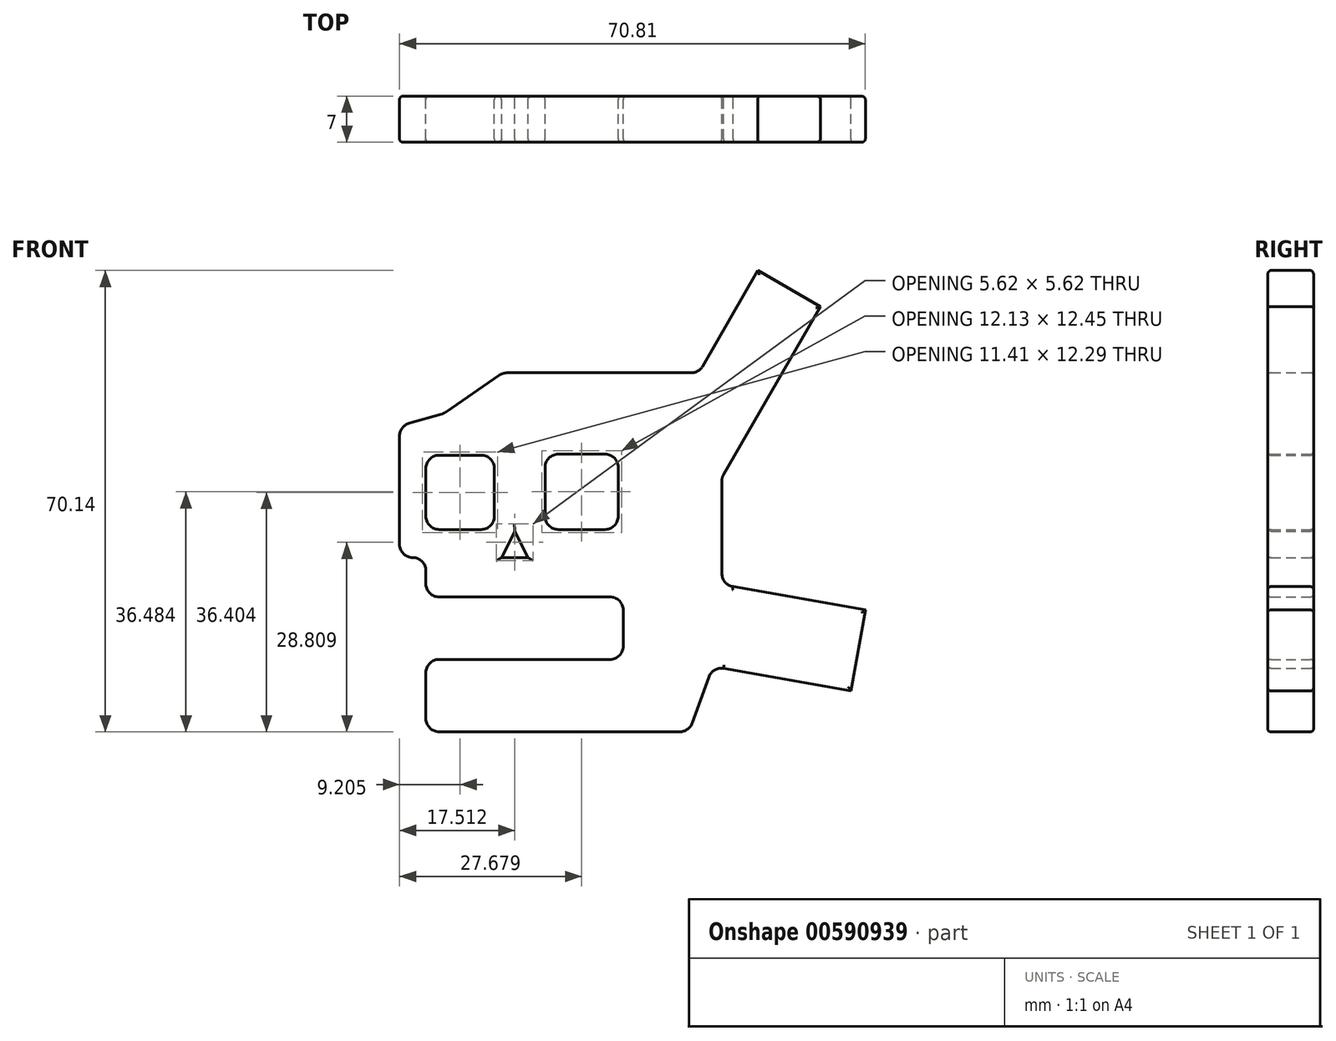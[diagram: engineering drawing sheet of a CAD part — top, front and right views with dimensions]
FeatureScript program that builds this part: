
annotation { "Feature Type Name" : "Feature", "Feature Type Description" : "" }
export const myFeature = defineFeature(function(context is Context, id is Id, definition is map)
    precondition{}
    {
        {
            var Q0;
            Q0=qCreatedBy(makeId("Front.planeOp"),FACE);
            var sketch = newSketch(context, id + "F0", { "sketchPlane" : qUnion([Q0])});
            skLineSegment(sketch, "E0", {"start": v(2, 0) * mm, "end": v(28, 0) * mm});
            skLineSegment(sketch, "E1", {"start": v(30, 2) * mm, "end": v(30, 7.5) * mm});
            skLineSegment(sketch, "E2", {"start": v(28, 9.5) * mm, "end": v(2, 9.5) * mm});
            skPoint(sketch, "E3.visualSharp", {"position": v(30, 9.5) * mm});
            skArc(sketch, "E3.filletArc", {"start": v(30, 7.5) * mm, "mid": v(29.41, 8.91) * mm, "end": v(28, 9.5) * mm});
            skPoint(sketch, "E4.visualSharp", {"position": v(30, 0) * mm});
            skArc(sketch, "E4.filletArc", {"start": v(28, 0) * mm, "mid": v(29.41, 0.59) * mm, "end": v(30, 2) * mm});
            skLineSegment(sketch, "E5", {"start": v(0, -2) * mm, "end": v(0, -9) * mm});
            skLineSegment(sketch, "E6", {"start": v(2, -11) * mm, "end": v(38.6, -11) * mm});
            skLineSegment(sketch, "E7", {"start": v(40.48, -9.68) * mm, "end": v(43.04, -2.66) * mm});
            skLineSegment(sketch, "E8", {"start": v(45, 13.04) * mm, "end": v(45, 27.12) * mm});
            skLineSegment(sketch, "E9", {"start": v(45.27, 28.12) * mm, "end": v(60, 53.64) * mm});
            skLineSegment(sketch, "E10", {"start": v(60, 53.64) * mm, "end": v(50.47, 59.14) * mm});
            skLineSegment(sketch, "E11", {"start": v(50.47, 59.14) * mm, "end": v(42.06, 44.57) * mm});
            skLineSegment(sketch, "E12", {"start": v(40.33, 43.57) * mm, "end": v(12.31, 43.57) * mm});
            skLineSegment(sketch, "E13", {"start": v(11.18, 43.22) * mm, "end": v(3.06, 37.63) * mm});
            skLineSegment(sketch, "E14", {"start": v(2.48, 37.35) * mm, "end": v(-2.55, 35.9) * mm});
            skLineSegment(sketch, "E15", {"start": v(-4, 33.98) * mm, "end": v(-4, 17.49) * mm});
            skLineSegment(sketch, "E16", {"start": v(-2, 15.49) * mm, "end": v(-2, 15.49) * mm});
            skPoint(sketch, "E17.end.orphan", {"position": v(0.1, 9.49) * mm});
            skLineSegment(sketch, "E18", {"start": v(0, 11.5) * mm, "end": v(0, 13.49) * mm});
            skPoint(sketch, "E19.orphan", {"position": v(0.1, 15.49) * mm});
            skLineSegment(sketch, "E20.bottom", {"start": v(2, 19.76) * mm, "end": v(8.41, 19.76) * mm});
            skLineSegment(sketch, "E20.top", {"start": v(2, 31.05) * mm, "end": v(8.41, 31.05) * mm});
            skLineSegment(sketch, "E20.left", {"start": v(0, 21.76) * mm, "end": v(0, 29.05) * mm});
            skLineSegment(sketch, "E20.right", {"start": v(10.41, 21.76) * mm, "end": v(10.41, 29.05) * mm});
            skLineSegment(sketch, "E21.bottom", {"start": v(20.12, 19.76) * mm, "end": v(27.24, 19.76) * mm});
            skLineSegment(sketch, "E21.top", {"start": v(20.12, 31.21) * mm, "end": v(27.24, 31.21) * mm});
            skLineSegment(sketch, "E21.left", {"start": v(18.12, 21.76) * mm, "end": v(18.12, 29.21) * mm});
            skLineSegment(sketch, "E21.right", {"start": v(29.24, 21.76) * mm, "end": v(29.24, 29.21) * mm});
            skLineSegment(sketch, "E22", {"start": v(13.48, 19.5) * mm, "end": v(11.5, 15.5) * mm});
            skLineSegment(sketch, "E23", {"start": v(11.5, 15.5) * mm, "end": v(15.5, 15.5) * mm});
            skLineSegment(sketch, "E24", {"start": v(15.5, 15.5) * mm, "end": v(13.48, 19.5) * mm});
            skPoint(sketch, "E25.visualSharp", {"position": v(29.24, 19.76) * mm});
            skArc(sketch, "E25.filletArc", {"start": v(27.24, 19.76) * mm, "mid": v(28.66, 20.34) * mm, "end": v(29.24, 21.76) * mm});
            skPoint(sketch, "E26.visualSharp", {"position": v(18.12, 19.76) * mm});
            skArc(sketch, "E26.filletArc", {"start": v(18.12, 21.76) * mm, "mid": v(18.7, 20.34) * mm, "end": v(20.12, 19.76) * mm});
            skPoint(sketch, "E27.visualSharp", {"position": v(29.24, 31.21) * mm});
            skArc(sketch, "E27.filletArc", {"start": v(29.24, 29.21) * mm, "mid": v(28.66, 30.62) * mm, "end": v(27.24, 31.21) * mm});
            skPoint(sketch, "E28.visualSharp", {"position": v(18.12, 31.21) * mm});
            skArc(sketch, "E28.filletArc", {"start": v(20.12, 31.21) * mm, "mid": v(18.7, 30.62) * mm, "end": v(18.12, 29.21) * mm});
            skPoint(sketch, "E29.visualSharp", {"position": v(10.41, 31.05) * mm});
            skArc(sketch, "E29.filletArc", {"start": v(10.41, 29.05) * mm, "mid": v(9.82, 30.46) * mm, "end": v(8.41, 31.05) * mm});
            skPoint(sketch, "E30.visualSharp", {"position": v(10.41, 19.76) * mm});
            skArc(sketch, "E30.filletArc", {"start": v(8.41, 19.76) * mm, "mid": v(9.82, 20.34) * mm, "end": v(10.41, 21.76) * mm});
            skPoint(sketch, "E31.visualSharp", {"position": v(0, 19.76) * mm});
            skArc(sketch, "E31.filletArc", {"start": v(0, 21.76) * mm, "mid": v(0.59, 20.34) * mm, "end": v(2, 19.76) * mm});
            skPoint(sketch, "E32.visualSharp", {"position": v(0, 31.05) * mm});
            skArc(sketch, "E32.filletArc", {"start": v(2, 31.05) * mm, "mid": v(0.59, 30.46) * mm, "end": v(0, 29.05) * mm});
            skPoint(sketch, "E33.visualSharp", {"position": v(-4, 15.49) * mm});
            skArc(sketch, "E33.filletArc", {"start": v(-4, 17.49) * mm, "mid": v(-3.41, 16.07) * mm, "end": v(-2, 15.49) * mm});
            skPoint(sketch, "E34.visualSharp", {"position": v(0, 15.49) * mm});
            skArc(sketch, "E34.filletArc", {"start": v(0, 13.49) * mm, "mid": v(-0.59, 14.9) * mm, "end": v(-2, 15.49) * mm});
            skPoint(sketch, "E35.visualSharp", {"position": v(-4, 35.49) * mm});
            skArc(sketch, "E35.filletArc", {"start": v(-2.55, 35.9) * mm, "mid": v(-3.6, 35.18) * mm, "end": v(-4, 33.98) * mm});
            skPoint(sketch, "E36.visualSharp", {"position": v(2.8, 37.44) * mm});
            skArc(sketch, "E36.filletArc", {"start": v(2.48, 37.35) * mm, "mid": v(2.78, 37.46) * mm, "end": v(3.06, 37.63) * mm});
            skPoint(sketch, "E37.visualSharp", {"position": v(11.69, 43.57) * mm});
            skArc(sketch, "E37.filletArc", {"start": v(12.31, 43.57) * mm, "mid": v(11.72, 43.48) * mm, "end": v(11.18, 43.22) * mm});
            skPoint(sketch, "E38.visualSharp", {"position": v(41.49, 43.57) * mm});
            skArc(sketch, "E38.filletArc", {"start": v(40.33, 43.57) * mm, "mid": v(41.33, 43.84) * mm, "end": v(42.06, 44.57) * mm});
            skPoint(sketch, "E39.visualSharp", {"position": v(45, 27.66) * mm});
            skArc(sketch, "E39.filletArc", {"start": v(45.27, 28.12) * mm, "mid": v(45.07, 27.64) * mm, "end": v(45, 27.12) * mm});
            skPoint(sketch, "E40.visualSharp", {"position": v(45, 12.8) * mm});
            skArc(sketch, "E40.filletArc", {"start": v(45, 13.04) * mm, "mid": v(45.48, 11.74) * mm, "end": v(46.7, 11.07) * mm});
            skPoint(sketch, "E41.visualSharp", {"position": v(47.97, 10.9) * mm});
            skArc(sketch, "E41.filletArc", {"start": v(45.24, -1.37) * mm, "mid": v(43.9, -1.62) * mm, "end": v(43.04, -2.66) * mm});
            skPoint(sketch, "E42.visualSharp", {"position": v(0, 0) * mm});
            skArc(sketch, "E42.filletArc", {"start": v(2, 0) * mm, "mid": v(0.59, -0.59) * mm, "end": v(0, -2) * mm});
            skPoint(sketch, "E43.visualSharp", {"position": v(0, -11) * mm});
            skArc(sketch, "E43.filletArc", {"start": v(0, -9) * mm, "mid": v(0.59, -10.41) * mm, "end": v(2, -11) * mm});
            skPoint(sketch, "E44.visualSharp", {"position": v(0, 9.5) * mm});
            skArc(sketch, "E44.filletArc", {"start": v(0, 11.5) * mm, "mid": v(0.59, 10.09) * mm, "end": v(2, 9.5) * mm});
            skPoint(sketch, "E45.visualSharp", {"position": v(40, -11) * mm});
            skArc(sketch, "E45.filletArc", {"start": v(38.6, -11) * mm, "mid": v(39.75, -10.64) * mm, "end": v(40.48, -9.68) * mm});
            skPoint(sketch, "E46.start.orphan", {"position": v(65, 12.8) * mm});
            skLineSegment(sketch, "E47", {"start": v(46.7, 11.07) * mm, "end": v(66.81, 7.52) * mm});
            skLineSegment(sketch, "E48", {"start": v(66.81, 7.52) * mm, "end": v(64.64, -4.8) * mm});
            skLineSegment(sketch, "E49", {"start": v(45.24, -1.37) * mm, "end": v(64.64, -4.8) * mm});
            skSolve(sketch);
        }
        {
            var Q0;
            Q0=qSketchRegion(id+"F0",true);
            extrude(context, id + "F1", {"entities" : qUnion([Q0]), "depth" : 7 * mm, "offsetDistance" : 25 * mm});
        }
        {
            var Q0;
            Q0=makeQuery(id+"F1.opExtrude","CAP_FACE",FACE,{"disambiguationData":[OSD([sQuery(id+"F0.wireOp",EDGE,"E0"),sQuery(id+"F0.wireOp",EDGE,"E1"),sQuery(id+"F0.wireOp",EDGE,"E2"),sQuery(id+"F0.wireOp",EDGE,"E3.filletArc"),sQuery(id+"F0.wireOp",EDGE,"E4.filletArc"),sQuery(id+"F0.wireOp",EDGE,"E5"),sQuery(id+"F0.wireOp",EDGE,"E6"),sQuery(id+"F0.wireOp",EDGE,"E7"),sQuery(id+"F0.wireOp",EDGE,"84da15e0-1c70-4c55-b333-23809a0905f5"),sQuery(id+"F0.wireOp",EDGE,"15dd962d-3710-4e93-ae30-5309a48b2760"),sQuery(id+"F0.wireOp",EDGE,"E46"),sQuery(id+"F0.wireOp",EDGE,"E8"),sQuery(id+"F0.wireOp",EDGE,"E9"),sQuery(id+"F0.wireOp",EDGE,"E10"),sQuery(id+"F0.wireOp",EDGE,"E11"),sQuery(id+"F0.wireOp",EDGE,"E12"),sQuery(id+"F0.wireOp",EDGE,"E13"),sQuery(id+"F0.wireOp",EDGE,"E14"),sQuery(id+"F0.wireOp",EDGE,"E15"),sQuery(id+"F0.wireOp",EDGE,"E18"),sQuery(id+"F0.wireOp",EDGE,"E20.bottom"),sQuery(id+"F0.wireOp",EDGE,"E20.top"),sQuery(id+"F0.wireOp",EDGE,"E20.left"),sQuery(id+"F0.wireOp",EDGE,"E20.right"),sQuery(id+"F0.wireOp",EDGE,"E21.bottom"),sQuery(id+"F0.wireOp",EDGE,"E21.top"),sQuery(id+"F0.wireOp",EDGE,"E21.left"),sQuery(id+"F0.wireOp",EDGE,"E21.right"),sQuery(id+"F0.wireOp",EDGE,"E22"),sQuery(id+"F0.wireOp",EDGE,"E23"),sQuery(id+"F0.wireOp",EDGE,"E24"),sQuery(id+"F0.wireOp",EDGE,"E25.filletArc"),sQuery(id+"F0.wireOp",EDGE,"E26.filletArc"),sQuery(id+"F0.wireOp",EDGE,"E27.filletArc"),sQuery(id+"F0.wireOp",EDGE,"E28.filletArc"),sQuery(id+"F0.wireOp",EDGE,"E29.filletArc"),sQuery(id+"F0.wireOp",EDGE,"E30.filletArc"),sQuery(id+"F0.wireOp",EDGE,"E31.filletArc"),sQuery(id+"F0.wireOp",EDGE,"E32.filletArc"),sQuery(id+"F0.wireOp",EDGE,"E33.filletArc"),sQuery(id+"F0.wireOp",EDGE,"E34.filletArc"),sQuery(id+"F0.wireOp",EDGE,"E35.filletArc"),sQuery(id+"F0.wireOp",EDGE,"E36.filletArc"),sQuery(id+"F0.wireOp",EDGE,"E37.filletArc"),sQuery(id+"F0.wireOp",EDGE,"E38.filletArc"),sQuery(id+"F0.wireOp",EDGE,"E39.filletArc"),sQuery(id+"F0.wireOp",EDGE,"E40.filletArc"),sQuery(id+"F0.wireOp",EDGE,"E41.filletArc"),sQuery(id+"F0.wireOp",EDGE,"E42.filletArc"),sQuery(id+"F0.wireOp",EDGE,"E43.filletArc"),sQuery(id+"F0.wireOp",EDGE,"E44.filletArc"),sQuery(id+"F0.wireOp",EDGE,"E45.filletArc")])],"isStart":false});
            var Q1;
            Q1=makeQuery(id+"F1.opExtrude","CAP_FACE",FACE,{"disambiguationData":[OSD([sQuery(id+"F0.wireOp",EDGE,"E0"),sQuery(id+"F0.wireOp",EDGE,"E1"),sQuery(id+"F0.wireOp",EDGE,"E2"),sQuery(id+"F0.wireOp",EDGE,"E3.filletArc"),sQuery(id+"F0.wireOp",EDGE,"E4.filletArc"),sQuery(id+"F0.wireOp",EDGE,"E5"),sQuery(id+"F0.wireOp",EDGE,"E6"),sQuery(id+"F0.wireOp",EDGE,"E7"),sQuery(id+"F0.wireOp",EDGE,"84da15e0-1c70-4c55-b333-23809a0905f5"),sQuery(id+"F0.wireOp",EDGE,"15dd962d-3710-4e93-ae30-5309a48b2760"),sQuery(id+"F0.wireOp",EDGE,"E46"),sQuery(id+"F0.wireOp",EDGE,"E8"),sQuery(id+"F0.wireOp",EDGE,"E9"),sQuery(id+"F0.wireOp",EDGE,"E10"),sQuery(id+"F0.wireOp",EDGE,"E11"),sQuery(id+"F0.wireOp",EDGE,"E12"),sQuery(id+"F0.wireOp",EDGE,"E13"),sQuery(id+"F0.wireOp",EDGE,"E14"),sQuery(id+"F0.wireOp",EDGE,"E15"),sQuery(id+"F0.wireOp",EDGE,"E18"),sQuery(id+"F0.wireOp",EDGE,"E20.bottom"),sQuery(id+"F0.wireOp",EDGE,"E20.top"),sQuery(id+"F0.wireOp",EDGE,"E20.left"),sQuery(id+"F0.wireOp",EDGE,"E20.right"),sQuery(id+"F0.wireOp",EDGE,"E21.bottom"),sQuery(id+"F0.wireOp",EDGE,"E21.top"),sQuery(id+"F0.wireOp",EDGE,"E21.left"),sQuery(id+"F0.wireOp",EDGE,"E21.right"),sQuery(id+"F0.wireOp",EDGE,"E22"),sQuery(id+"F0.wireOp",EDGE,"E23"),sQuery(id+"F0.wireOp",EDGE,"E24"),sQuery(id+"F0.wireOp",EDGE,"E25.filletArc"),sQuery(id+"F0.wireOp",EDGE,"E26.filletArc"),sQuery(id+"F0.wireOp",EDGE,"E27.filletArc"),sQuery(id+"F0.wireOp",EDGE,"E28.filletArc"),sQuery(id+"F0.wireOp",EDGE,"E29.filletArc"),sQuery(id+"F0.wireOp",EDGE,"E30.filletArc"),sQuery(id+"F0.wireOp",EDGE,"E31.filletArc"),sQuery(id+"F0.wireOp",EDGE,"E32.filletArc"),sQuery(id+"F0.wireOp",EDGE,"E33.filletArc"),sQuery(id+"F0.wireOp",EDGE,"E34.filletArc"),sQuery(id+"F0.wireOp",EDGE,"E35.filletArc"),sQuery(id+"F0.wireOp",EDGE,"E36.filletArc"),sQuery(id+"F0.wireOp",EDGE,"E37.filletArc"),sQuery(id+"F0.wireOp",EDGE,"E38.filletArc"),sQuery(id+"F0.wireOp",EDGE,"E39.filletArc"),sQuery(id+"F0.wireOp",EDGE,"E40.filletArc"),sQuery(id+"F0.wireOp",EDGE,"E41.filletArc"),sQuery(id+"F0.wireOp",EDGE,"E42.filletArc"),sQuery(id+"F0.wireOp",EDGE,"E43.filletArc"),sQuery(id+"F0.wireOp",EDGE,"E44.filletArc"),sQuery(id+"F0.wireOp",EDGE,"E45.filletArc")])],"isStart":true});
            fillet(context, id + "F2", {"entities" : qUnion([Q0, Q1]), "radius" : .5 * mm, "tangentPropagation" : true, "allowEdgeOverflow" : false});
        }
    });
